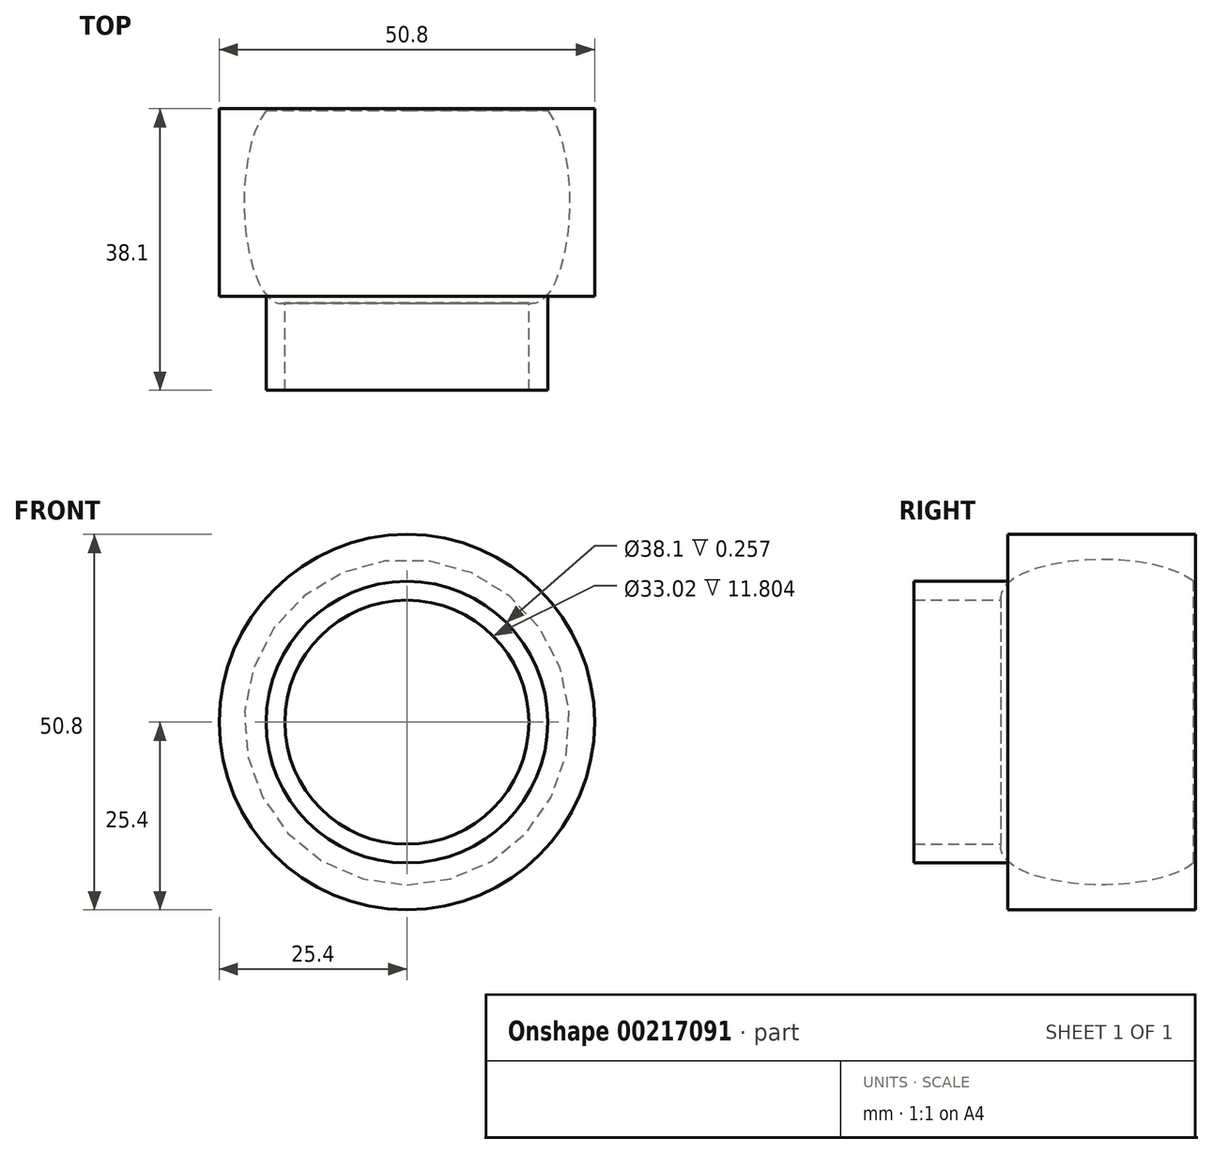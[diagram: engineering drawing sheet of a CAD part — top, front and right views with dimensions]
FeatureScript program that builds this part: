
annotation { "Feature Type Name" : "Feature", "Feature Type Description" : "" }
export const myFeature = defineFeature(function(context is Context, id is Id, definition is map)
    precondition{}
    {
        {
            var Q0;
            Q0=qCreatedBy(makeId("Front.planeOp"),FACE);
            var sketch = newSketch(context, id + "F0", { "sketchPlane" : qUnion([Q0])});
            skCircle(sketch, "E0", {"center": v(0, 0) * mm, "radius": 19.05 * mm});
            skCircle(sketch, "E1", {"center": v(0, 0) * mm, "radius": 25.4 * mm});
            skCircle(sketch, "E2.0", {"center": v(0, 0) * mm, "radius": 16.51 * mm});
            skSolve(sketch);
        }
        {
            var Q0;
            Q0=makeQuery(id+"F0.imprint","IMPRINT",FACE,{"disambiguationData":[TD([[makeQuery(id+"F0.imprint","IMPRINT",EDGE,{"derivedFrom":sQuery(id+"F0.wireOp",EDGE,"E0")}),-1.0]])]});
            extrude(context, id + "F1", {"entities" : qUnion([Q0]), "depth" : 25.4 * mm, "symmetric" : true});
        }
        {
            var Q0;
            Q0=makeQuery(id+"F0.imprint","IMPRINT",FACE,{"disambiguationData":[TD([[makeQuery(id+"F0.imprint","IMPRINT",EDGE,{"derivedFrom":sQuery(id+"F0.wireOp",EDGE,"E0")}),1.0]])]});
            extrude(context, id + "F2", {"entities" : qUnion([Q0]), "operationType" : NewBodyOperationType.ADD, "depth" : 25.4 * mm});
        }
        {
            var Q0;
            Q0=qCreatedBy(makeId("Right.planeOp"),FACE);
            var sketch = newSketch(context, id + "F3", { "sketchPlane" : qUnion([Q0])});
            skEllipse(sketch, "E3", {"center": v(0, 16.98) * mm, "majorRadius": 13.65 * mm, "minorRadius": 5.04 * mm, "majorAxis": v(1, 0)});
            skSolve(sketch);
        }
        {
            var Q0;
            Q0 = qSketchRegion(id + "F3", true);
            var Q1;
            Q1=makeQuery(id+"F1.opExtrude","CAP_EDGE",EDGE,{"disambiguationData":[OSD([sQuery(id+"F0.wireOp",EDGE,"E0")])],"isStart":true});
            revolve(context, id + "F4", {"operationType" : NewBodyOperationType.REMOVE, "entities" : qUnion([Q0]), "axis" : qUnion([Q1]), "revolveType" : RevolveType.FULL, "oppositeDirection" : true});
        }
    });
